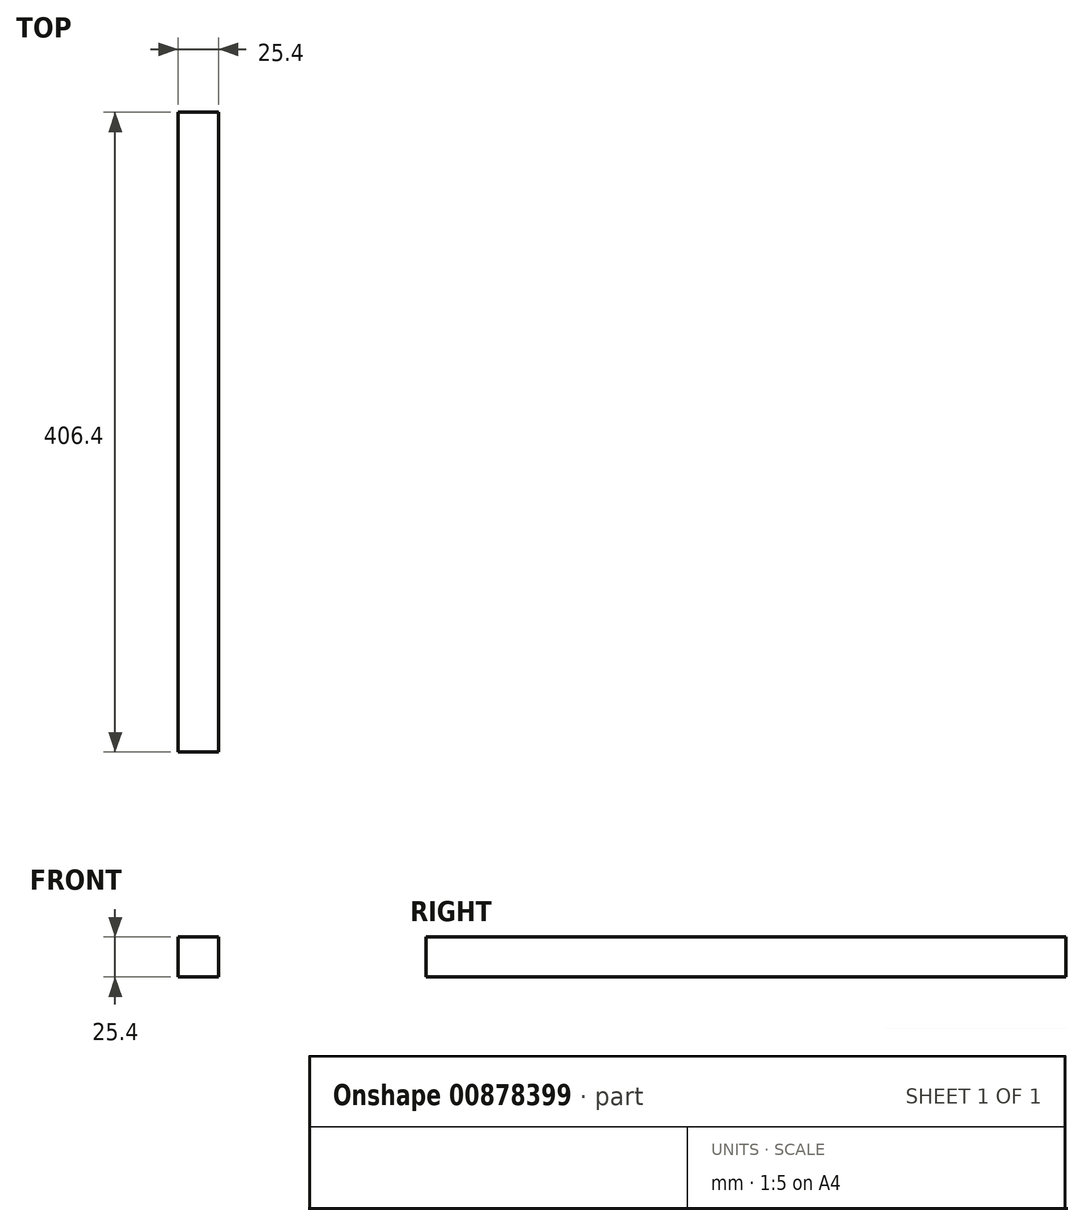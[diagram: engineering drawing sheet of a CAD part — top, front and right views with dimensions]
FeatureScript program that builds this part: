
annotation { "Feature Type Name" : "Feature", "Feature Type Description" : "" }
export const myFeature = defineFeature(function(context is Context, id is Id, definition is map)
    precondition{}
    {
        {
            var Q0;
            Q0=qCreatedBy(makeId("Top.planeOp"),FACE);
            var sketch = newSketch(context, id + "F0", { "sketchPlane" : qUnion([Q0])});
            skLineSegment(sketch, "E0.bottom", {"start": v(0, 0) * mm, "end": v(25.4, 0) * mm});
            skLineSegment(sketch, "E0.top", {"start": v(0, 406.4) * mm, "end": v(25.4, 406.4) * mm});
            skLineSegment(sketch, "E0.left", {"start": v(0, 0) * mm, "end": v(0, 406.4) * mm});
            skLineSegment(sketch, "E0.right", {"start": v(25.4, 0) * mm, "end": v(25.4, 406.4) * mm});
            skSolve(sketch);
        }
        {
            var Q0;
            Q0=makeQuery(id+"F0.imprint","IMPRINT",FACE,{"disambiguationData":[TD([[makeQuery(id+"F0.imprint","IMPRINT",EDGE,{"derivedFrom":sQuery(id+"F0.wireOp",EDGE,"E0.bottom")}),1.0]])]});
            extrude(context, id + "F1", {"entities" : qUnion([Q0]), "depth" : 25.4 * mm, "offsetDistance" : 25.4 * mm});
        }
    });
